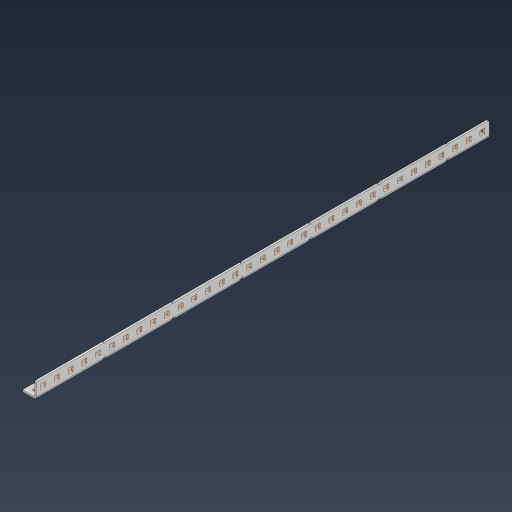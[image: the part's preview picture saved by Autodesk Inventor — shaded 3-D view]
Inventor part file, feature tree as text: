
AUTODESK INVENTOR PART (.ipt)
format: ipt  version: 2024.3 (Build 283343000, 343)  size: 1,209,856 bytes
history: native  units: in
note: dims shown in document units (in); Inventor stores cm internally (conversion verified against a paired STEP export)
features: other x106, extrude x97, sheet_metal_op x11, pattern_linear x2, mirror x1, chamfer x1, sketch x1
ambient origin geometry x8: Origin, YZ Plane, XZ Plane, XY Plane, X Axis, Y Axis, Z Axis, Center Point
bodies: Solid1 (feature_tree), Body (feature_tree)
feature tree (219):
  sheet_metal_op  "Flanges"
  other  "Flange Pattern Plane"
  other  "Flange Pattern Sketch"
  sheet_metal_op  "Flange Pattern"
  sheet_metal_op  "Body Pattern"
  pattern_linear  "Center Pattern"  Spacing1=16.5in  [1 undecoded]
  other  "Arc Length"
  mirror  "Notch Mirror"
  pattern_linear  "Notch Pattern"  Spacing1=0.0625in  [1 undecoded]
  chamfer  "End Chamfer"
  extrude  "Half Cut"  Depth=0.0625in
  other  "Plate1"
  sketch  "Sketch2"  dims[d0=1.0in d1=16.5in d2=0.0625in d3=0.0625in d4=0.0312in d5=0.125in d6=0.0625in d7=0.5in d8=90.0deg d9=0.0312in d10=0.25in d11=0.0625in d12=0.0625in d16=0.182in d17=0.02in d18=0.0625in d19=0.0in d20=0.25in d21=0.25in d38=12.9921in d40=0.5in d41=0.3937in d43=1.0in d46=0.172in d47=1.0in d48=0.0in d49=0.182in d50=0.02in d51=0.25in d52=0.25in d53=0.0625in d54=0.0in d55=0.172in d56=1.0in d57=0.0in d58=0.25in d60=12.9921in d62=0.5in d63=0.3937in d65=0.5in d85=0.1473in d86=0.1782in d88=0.04in d89=0.0625in d90=0.0in d91=0.04in d92=0.0491in d95=2.5in d96=0.04in d97=0.25in d98=45.0deg d99=0.25in d100=0.5in d101=0.0in d102=2.497in d106=0.182in d107=0.02in d108=0.5in d109=0.5in d110=0.0625in d111=0.0in d112=0.172in d113=0.5in d114=0.0in d117=0.5in d118=0.5in d119=0.5in]
  other  "Plate2"
  sheet_metal_op  "Bend1"
  sheet_metal_op  "Corner1"
  other  "Srf1"
  other  "Srf2"
  other  "Srf91"
  sheet_metal_op  "Body Pattern Sketch"
  other  "Srf92"
  other  "Srf786"
  other  "Srf823"
  other  "Srf824"
  other  "Srf825"
  other  "Srf826"
  other  "Srf827"
  other  "Srf828"
  other  "Srf829"
  other  "Srf856"
  other  "Srf857"
  other  "Srf858"
  other  "Srf859"
  other  "Srf860"
  other  "Srf861"
  other  "Srf862"
  other  "Srf889"
  other  "Srf890"
  other  "Srf891"
  other  "Srf892"
  other  "Srf893"
  other  "Srf894"
  other  "Srf895"
  other  "Srf896"
  other  "Srf922"
  other  "Srf923"
  other  "Srf924"
  other  "Srf925"
  other  "Srf926"
  other  "Srf959"
  other  "Srf960"
  other  "Srf961"
  other  "Srf962"
  other  "Srf963"
  other  "Srf996"
  other  "Srf997"
  other  "Srf998"
  other  "Srf999"
  other  "Srf1000"
  other  "Srf1143"
  other  "Srf1144"
  other  "Srf1145"
  other  "Srf1146"
  other  "Srf1147"
  other  "Srf1148"
  other  "Srf1149"
  other  "Srf1150"
  other  "Srf1151"
  other  "Srf1152"
  other  "Srf1153"
  other  "Srf1154"
  other  "Srf1155"
  other  "Srf1156"
  other  "Srf1157"
  other  "Srf1158"
  other  "Srf1159"
  other  "Srf1160"
  other  "Srf1161"
  other  "Srf1199"
  other  "Srf1200"
  other  "Srf1201"
  other  "Srf1202"
  other  "Srf1203"
  other  "Srf1204"
  other  "Srf1205"
  other  "Srf1206"
  other  "Srf1207"
  other  "Srf1208"
  other  "Srf1209"
  other  "Srf1210"
  other  "Srf1211"
  other  "Srf1212"
  other  "Srf1213"
  other  "Srf1214"
  other  "Srf1215"
  other  "Srf1216"
  other  "Srf1217"
  other  "Srf1255"
  other  "Srf1256"
  other  "Srf1257"
  other  "Srf1258"
  other  "Srf1259"
  other  "Srf1260"
  other  "Srf1261"
  other  "Srf1262"
  other  "Srf1263"
  other  "Srf1264"
  other  "Srf1265"
  other  "Srf1266"
  other  "Srf1267"
  other  "Srf1268"
  other  "Srf1269"
  other  "Srf1270"
  other  "Srf1271"
  other  "Srf1272"
  other  "Srf1273"
  sheet_metal_op  "Flange Stamp"
  sheet_metal_op  "Flange Circle"
  sheet_metal_op  "Body Stamp"
  sheet_metal_op  "Body Circle"
  other  "Center Stamp"
  other  "Center Circle"
  sheet_metal_op  "Notch"
  extrude  "ExtrusionSrf2"  Depth=0.0312in
  extrude  "ExtrusionSrf92"  Depth=0.5in
  extrude  "ExtrusionSrf823"  Depth=0.0625in
  extrude  "ExtrusionSrf824"  Depth=0.5in TaperAngle=90.0deg
  extrude  "ExtrusionSrf825"  Depth=0.5in
  extrude  "ExtrusionSrf826"  Depth=0.0625in
  extrude  "ExtrusionSrf827"  Depth=0.0625in
  extrude  "ExtrusionSrf828"  Depth=0.182in
  extrude  "ExtrusionSrf829"  Depth=0.02in
  extrude  "ExtrusionSrf856"  Depth=0.0625in
  extrude  "ExtrusionSrf857"  TaperAngle=0.0deg  [1 undecoded]
  extrude  "ExtrusionSrf858"  Depth=0.5in
  extrude  "ExtrusionSrf859"  Depth=0.5in
  extrude  "ExtrusionSrf860"  Depth=0.5in
  extrude  "ExtrusionSrf861"  Depth=0.5in
  extrude  "ExtrusionSrf862"  Depth=1.0in TaperAngle=0.0deg
  extrude  "ExtrusionSrf889"  Depth=0.182in
  extrude  "ExtrusionSrf890"  Depth=0.02in
  extrude  "ExtrusionSrf891"  Depth=0.5in
  extrude  "ExtrusionSrf892"  Depth=0.5in
  extrude  "ExtrusionSrf893"  Depth=0.0625in
  extrude  "ExtrusionSrf894"  TaperAngle=0.0deg  [1 undecoded]
  extrude  "ExtrusionSrf895"  Depth=0.5in
  extrude  "ExtrusionSrf896"  Depth=1.0in TaperAngle=0.0deg
  extrude  "ExtrusionSrf922"  Depth=0.5in
  extrude  "ExtrusionSrf923"  Depth=0.5in
  extrude  "ExtrusionSrf924"  Depth=0.5in
  extrude  "ExtrusionSrf925"  Depth=0.5in
  extrude  "ExtrusionSrf926"  Depth=0.5in
  extrude  "ExtrusionSrf959"  Depth=0.5in
  extrude  "ExtrusionSrf960"  Depth=0.0625in
  extrude  "ExtrusionSrf961"  TaperAngle=0.0deg  [1 undecoded]
  extrude  "ExtrusionSrf962"  Depth=0.5in
  extrude  "ExtrusionSrf963"  Depth=0.5in
  extrude  "ExtrusionSrf996"  Depth=0.5in
  extrude  "ExtrusionSrf997"  Depth=0.5in TaperAngle=45.0deg
  extrude  "ExtrusionSrf998"  Depth=0.5in
  extrude  "ExtrusionSrf999"  Depth=0.5in TaperAngle=0.0deg
  extrude  "ExtrusionSrf1000"  Depth=0.5in
  extrude  "ExtrusionSrf1143"  Depth=0.182in
  extrude  "ExtrusionSrf1144"  Depth=0.02in
  extrude  "ExtrusionSrf1145"  Depth=0.5in
  extrude  "ExtrusionSrf1146"  Depth=0.5in
  extrude  "ExtrusionSrf1147"  Depth=0.0625in
  extrude  "ExtrusionSrf1148"  TaperAngle=0.0deg  [1 undecoded]
  extrude  "ExtrusionSrf1149"  Depth=0.5in
  extrude  "ExtrusionSrf1150"  Depth=0.5in TaperAngle=0.0deg
  extrude  "ExtrusionSrf1151"  Depth=0.5in
  extrude  "ExtrusionSrf1152"  Depth=0.5in
  extrude  "ExtrusionSrf1153"  Depth=0.5in
  extrude  "ExtrusionSrf1154"  [1 undecoded]
  extrude  "ExtrusionSrf1155"  [1 undecoded]
  extrude  "ExtrusionSrf1156"  [1 undecoded]
  extrude  "ExtrusionSrf1157"  [1 undecoded]
  extrude  "ExtrusionSrf1158"  [1 undecoded]
  extrude  "ExtrusionSrf1159"  [1 undecoded]
  extrude  "ExtrusionSrf1160"  [1 undecoded]
  extrude  "ExtrusionSrf1161"  [1 undecoded]
  extrude  "ExtrusionSrf1199"  [1 undecoded]
  extrude  "ExtrusionSrf1200"  [1 undecoded]
  extrude  "ExtrusionSrf1201"  [1 undecoded]
  extrude  "ExtrusionSrf1202"  [1 undecoded]
  extrude  "ExtrusionSrf1203"  [1 undecoded]
  extrude  "ExtrusionSrf1204"  [1 undecoded]
  extrude  "ExtrusionSrf1205"  [1 undecoded]
  extrude  "ExtrusionSrf1206"  [1 undecoded]
  extrude  "ExtrusionSrf1207"  [1 undecoded]
  extrude  "ExtrusionSrf1208"  [1 undecoded]
  extrude  "ExtrusionSrf1209"  [1 undecoded]
  extrude  "ExtrusionSrf1210"  [1 undecoded]
  extrude  "ExtrusionSrf1211"  [1 undecoded]
  extrude  "ExtrusionSrf1212"  [1 undecoded]
  extrude  "ExtrusionSrf1213"  [1 undecoded]
  extrude  "ExtrusionSrf1214"  [1 undecoded]
  extrude  "ExtrusionSrf1215"  [1 undecoded]
  extrude  "ExtrusionSrf1216"  [1 undecoded]
  extrude  "ExtrusionSrf1217"  [1 undecoded]
  extrude  "ExtrusionSrf1255"  [1 undecoded]
  extrude  "ExtrusionSrf1256"  [1 undecoded]
  extrude  "ExtrusionSrf1257"  [1 undecoded]
  extrude  "ExtrusionSrf1258"  [1 undecoded]
  extrude  "ExtrusionSrf1259"  [1 undecoded]
  extrude  "ExtrusionSrf1260"  [1 undecoded]
  extrude  "ExtrusionSrf1261"  [1 undecoded]
  extrude  "ExtrusionSrf1262"  [1 undecoded]
  extrude  "ExtrusionSrf1263"  [1 undecoded]
  extrude  "ExtrusionSrf1264"  [1 undecoded]
  extrude  "ExtrusionSrf1265"  [1 undecoded]
  extrude  "ExtrusionSrf1266"  [1 undecoded]
  extrude  "ExtrusionSrf1267"  [1 undecoded]
  extrude  "ExtrusionSrf1268"  [1 undecoded]
  extrude  "ExtrusionSrf1269"  [1 undecoded]
  extrude  "ExtrusionSrf1270"  [1 undecoded]
  extrude  "ExtrusionSrf1271"  [1 undecoded]
  extrude  "ExtrusionSrf1272"  [1 undecoded]
  extrude  "ExtrusionSrf1273"  [1 undecoded]
note: 52 required parameter values undecoded (feature->parameter linkage not recoverable at this tier; creation-order binding heuristic only, values carry confidence <= 0.55)
